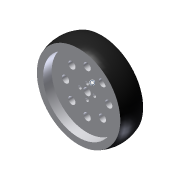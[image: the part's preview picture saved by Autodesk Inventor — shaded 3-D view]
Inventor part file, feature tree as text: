
AUTODESK INVENTOR PART (.ipt)
format: ipt  version: 2013 (Build 170138000, 138)  size: 144,384 bytes
history: native  units: in
note: dims shown in document units (in); Inventor stores cm internally (conversion verified against a paired STEP export)
features: other x4, plane x1
ambient origin geometry x8: Origin, YZ Plane, XZ Plane, XY Plane, X Axis, Y Axis, Z Axis, Center Point
bodies: Solid1 (feature_tree)
feature tree (5):
  other  "Tetrix wheel 4 in.ipt"
  other  "WHEEL_101MM_4-IN_2011::Tetrix wheel 4 in.ipt"
  other  "TaggingFeature1"
  plane  "Work Plane1"
  other  "iComposite:1"
